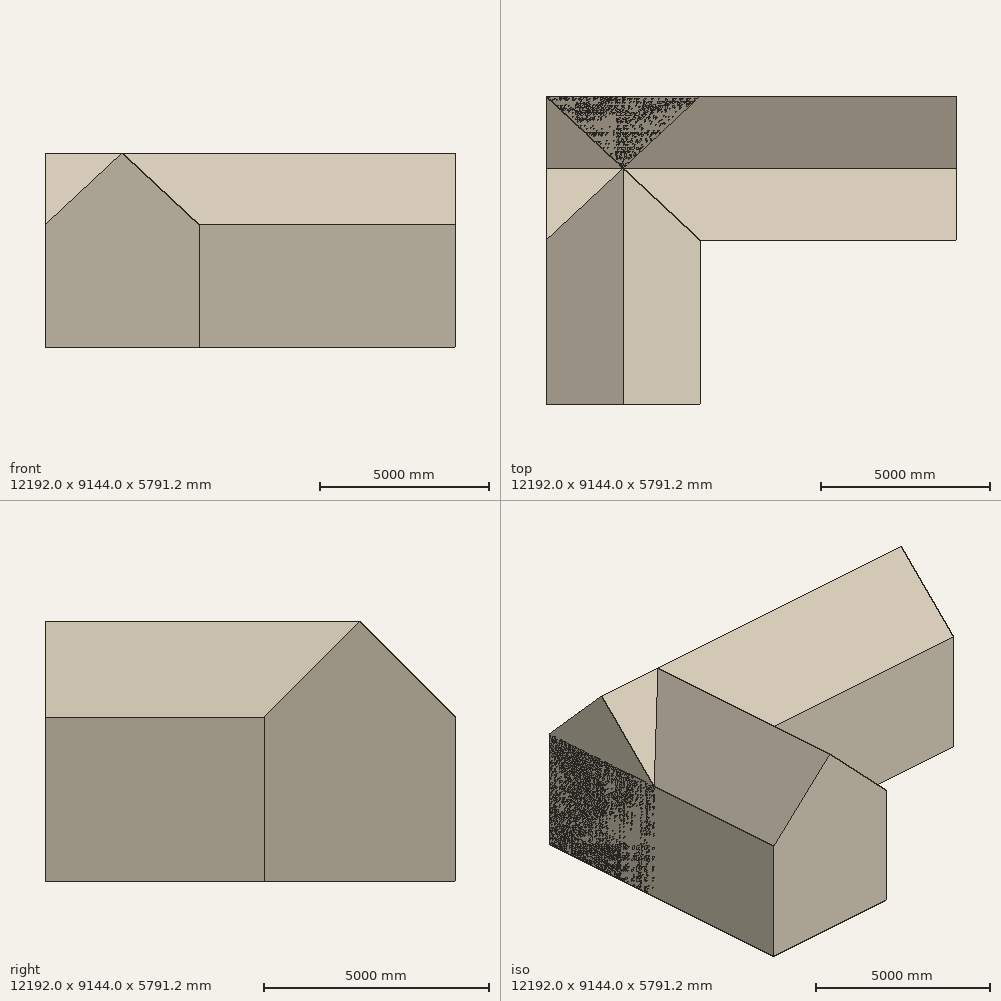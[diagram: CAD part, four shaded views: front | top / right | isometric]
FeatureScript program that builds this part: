
annotation { "Feature Type Name" : "Feature", "Feature Type Description" : "" }
export const myFeature = defineFeature(function(context is Context, id is Id, definition is map)
    precondition{}
    {
        {
            var Q0;
            Q0=qCreatedBy(makeId("Right.planeOp"),FACE);
            var sketch = newSketch(context, id + "F0", { "sketchPlane" : qUnion([Q0])});
            skLineSegment(sketch, "E0", {"start": v(0, 0) * mm, "end": v(0, 3657.6) * mm});
            skLineSegment(sketch, "E1", {"start": v(0, 3657.6) * mm, "end": v(2133.6, 5791.2) * mm});
            skLineSegment(sketch, "E2", {"start": v(2133.6, 5791.2) * mm, "end": v(4267.2, 3657.6) * mm});
            skLineSegment(sketch, "E3", {"start": v(4267.2, 3657.6) * mm, "end": v(4267.2, 0) * mm});
            skLineSegment(sketch, "E4", {"start": v(4267.2, 0) * mm, "end": v(0, 0) * mm});
            skLineSegment(sketch, "E5", {"start": v(0, 3657.6) * mm, "end": v(4267.2, 3657.6) * mm, "construction": true});
            skLineSegment(sketch, "E6", {"start": v(2133.6, 5791.2) * mm, "end": v(2133.6, 3657.6) * mm, "construction": true});
            skSolve(sketch);
        }
        {
            var Q0;
            Q0 = qSketchRegion(id + "F0", true);
            extrude(context, id + "F1", {"entities" : qUnion([Q0]), "depth" : 12192 * mm});
        }
        {
            var Q0;
            Q0=makeQuery(id+"F1.opExtrude","SWEPT_FACE",FACE,{"disambiguationData":[OSD([sQuery(id+"F0.wireOp",EDGE,"E0")])]});
            var sketch = newSketch(context, id + "F2", { "sketchPlane" : qUnion([Q0])});
            skLineSegment(sketch, "E7", {"start": v(0, 0) * mm, "end": v(0, 3657.6) * mm});
            skLineSegment(sketch, "E8", {"start": v(0, 3657.6) * mm, "end": v(2286, 5791.2) * mm});
            skLineSegment(sketch, "E9", {"start": v(2286, 5791.2) * mm, "end": v(4572, 3657.6) * mm});
            skLineSegment(sketch, "E10", {"start": v(4572, 3657.6) * mm, "end": v(4572, 0) * mm});
            skLineSegment(sketch, "E11", {"start": v(4572, 0) * mm, "end": v(0, 0) * mm});
            skLineSegment(sketch, "E12", {"start": v(0, 3657.6) * mm, "end": v(4572, 3657.6) * mm, "construction": true});
            skLineSegment(sketch, "E13", {"start": v(2286, 5791.2) * mm, "end": v(2286, 3657.6) * mm, "construction": true});
            skSolve(sketch);
        }
        {
            var Q0;
            Q0 = qSketchRegion(id + "F2", true);
            var Q1;
            Q1=sQuery(id+"F2.wireOp",EDGE,"E13");
            var Q2;
            Q2=sQuery(id+"F2.wireOp",EDGE,"E12");
            var Q3;
            Q3=makeQuery(id+"F1.opExtrude","SWEPT_BODY",BODY,{"disambiguationData":[OSD([sQuery(id+"F0.wireOp",EDGE,"E0"),sQuery(id+"F0.wireOp",EDGE,"E1"),sQuery(id+"F0.wireOp",EDGE,"E2"),sQuery(id+"F0.wireOp",EDGE,"E3"),sQuery(id+"F0.wireOp",EDGE,"E4")])]});
            extrude(context, id + "F3", {"entities" : qUnion([Q0]), "surfaceEntities" : qUnion([Q1, Q2]), "endBound" : BoundingType.UP_TO_BODY, "oppositeDirection" : true, "endBoundEntityBody" : qUnion([Q3]), "depth" : 25.4 * mm, "hasSecondDirection" : true, "secondDirectionOppositeDirection" : false, "secondDirectionDepth" : 4876.8 * mm});
        }
    });
